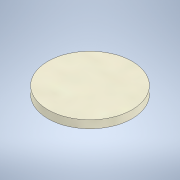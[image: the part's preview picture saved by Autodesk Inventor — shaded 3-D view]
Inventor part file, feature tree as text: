
AUTODESK INVENTOR PART (.ipt)
format: ipt  version: 2021 (Build 250183000, 183)  size: 97,280 bytes
history: native  units: mm
features: extrude x1, sketch x1
ambient origin geometry x8: Origin, YZ Plane, XZ Plane, XY Plane, X Axis, Y Axis, Z Axis, Center Point
bodies: Solid1 (feature_tree)
feature tree (2):
  extrude  "Extrusion1"  Depth=1.75mm TaperAngle=0.0deg
  sketch  "Sketch1"  dims[d0=18.9mm d1=1.75mm d2=0.0mm]
